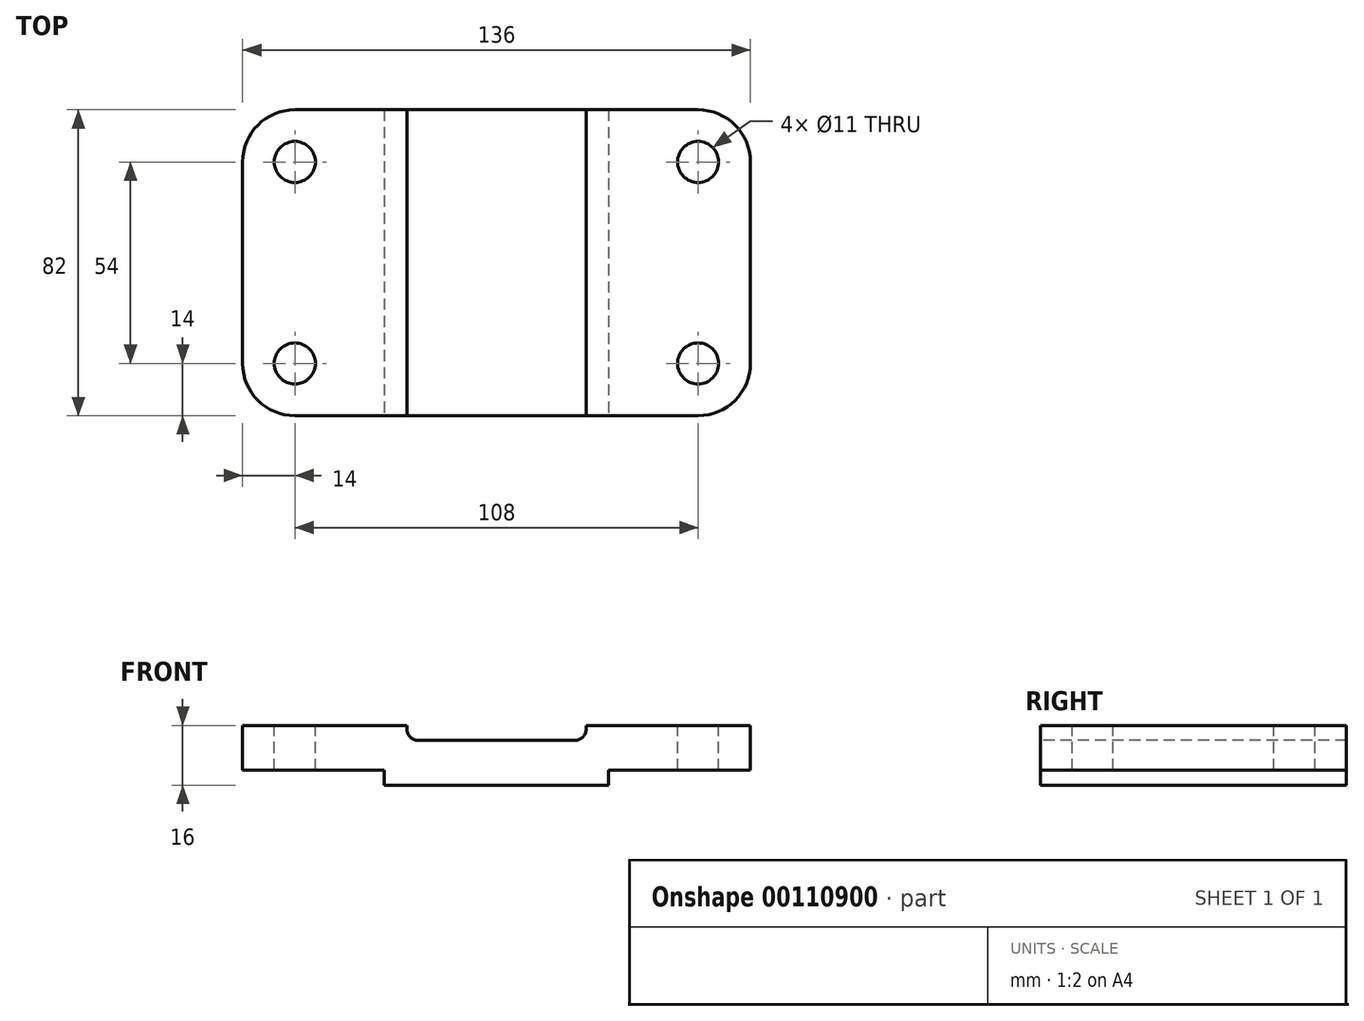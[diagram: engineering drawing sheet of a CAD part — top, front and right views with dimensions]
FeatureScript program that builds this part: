
annotation { "Feature Type Name" : "Feature", "Feature Type Description" : "" }
export const myFeature = defineFeature(function(context is Context, id is Id, definition is map)
    precondition{}
    {
        {
            var Q0;
            Q0=qCreatedBy(makeId("Top.planeOp"),FACE);
            var sketch = newSketch(context, id + "F0", { "sketchPlane" : qUnion([Q0])});
            skLineSegment(sketch, "E0.bottom", {"start": v(-14, 0) * mm, "end": v(-122, 0) * mm});
            skLineSegment(sketch, "E0.top", {"start": v(-14, 82) * mm, "end": v(-122, 82) * mm});
            skLineSegment(sketch, "E0.left", {"start": v(0, 14) * mm, "end": v(0, 68) * mm});
            skLineSegment(sketch, "E0.right", {"start": v(-136, 14) * mm, "end": v(-136, 68) * mm});
            skPoint(sketch, "E1.visualSharp", {"position": v(-136, 82) * mm});
            skArc(sketch, "E1.filletArc", {"start": v(-122, 82) * mm, "mid": v(-131.9, 77.9) * mm, "end": v(-136, 68) * mm});
            skPoint(sketch, "E2.visualSharp", {"position": v(0, 82) * mm});
            skArc(sketch, "E2.filletArc", {"start": v(0, 68) * mm, "mid": v(-4.1, 77.9) * mm, "end": v(-14, 82) * mm});
            skPoint(sketch, "E3.visualSharp", {"position": v(0, 0) * mm});
            skArc(sketch, "E3.filletArc", {"start": v(-14, 0) * mm, "mid": v(-4.1, 4.1) * mm, "end": v(0, 14) * mm});
            skPoint(sketch, "E4.visualSharp", {"position": v(-136, 0) * mm});
            skArc(sketch, "E4.filletArc", {"start": v(-136, 14) * mm, "mid": v(-131.9, 4.1) * mm, "end": v(-122, 0) * mm});
            skCircle(sketch, "E5", {"center": v(-122, 68) * mm, "radius": 5.5 * mm});
            skCircle(sketch, "E6.0.1.0", {"center": v(-122, 14) * mm, "radius": 5.5 * mm});
            skCircle(sketch, "E6.1.0.0", {"center": v(-14, 68) * mm, "radius": 5.5 * mm});
            skCircle(sketch, "E6.1.1.0", {"center": v(-14, 14) * mm, "radius": 5.5 * mm});
            skLineSegment(sketch, "E6.direction1", {"start": v(-122, 68) * mm, "end": v(-14, 68) * mm, "construction": true});
            skLineSegment(sketch, "E6.direction2", {"start": v(-122, 68) * mm, "end": v(-122, 14) * mm, "construction": true});
            skSolve(sketch);
        }
        {
            var Q0;
            Q0=makeQuery(id+"F0.imprint","IMPRINT",FACE,{"disambiguationData":[TD([[makeQuery(id+"F0.imprint","IMPRINT",EDGE,{"derivedFrom":sQuery(id+"F0.wireOp",EDGE,"E0.bottom")}),-1.0]])]});
            extrude(context, id + "F1", {"entities" : qUnion([Q0]), "oppositeDirection" : true, "depth" : 16 * mm});
        }
        {
            var Q0;
            Q0=makeQuery(id+"F1.opExtrude","SWEPT_FACE",FACE,{"disambiguationData":[OSD([sQuery(id+"F0.wireOp",EDGE,"E0.bottom")])]});
            var sketch = newSketch(context, id + "F2", { "sketchPlane" : qUnion([Q0])});
            skLineSegment(sketch, "E7", {"start": v(0, 0) * mm, "end": v(-44, 0) * mm});
            skLineSegment(sketch, "E8", {"start": v(-44, 0) * mm, "end": v(-44, -1) * mm});
            skLineSegment(sketch, "E9", {"start": v(-47, -4) * mm, "end": v(-89, -4) * mm});
            skLineSegment(sketch, "E10", {"start": v(-92, -1) * mm, "end": v(-92, 0) * mm});
            skLineSegment(sketch, "E11", {"start": v(-92, 0) * mm, "end": v(-136, 0) * mm});
            skPoint(sketch, "E12.visualSharp", {"position": v(-92, -4) * mm});
            skArc(sketch, "E12.filletArc", {"start": v(-92, -1) * mm, "mid": v(-91.12, -3.12) * mm, "end": v(-89, -4) * mm});
            skPoint(sketch, "E13.visualSharp", {"position": v(-44, -4) * mm});
            skArc(sketch, "E13.filletArc", {"start": v(-47, -4) * mm, "mid": v(-44.88, -3.12) * mm, "end": v(-44, -1) * mm});
            skLineSegment(sketch, "E14", {"start": v(-136, -12) * mm, "end": v(-98, -12) * mm});
            skLineSegment(sketch, "E15", {"start": v(-98, -12) * mm, "end": v(-98, -16) * mm});
            skLineSegment(sketch, "E16", {"start": v(-98, -16) * mm, "end": v(-38, -16) * mm});
            skLineSegment(sketch, "E17", {"start": v(-38, -16) * mm, "end": v(-38, -12) * mm});
            skLineSegment(sketch, "E18", {"start": v(-38, -12) * mm, "end": v(0, -12) * mm});
            skLineSegment(sketch, "E19", {"start": v(-136, 0) * mm, "end": v(-136, -12) * mm});
            skLineSegment(sketch, "E20", {"start": v(0, 0) * mm, "end": v(0, -12) * mm});
            skLineSegment(sketch, "E21", {"start": v(-136, -12) * mm, "end": v(-136, -16) * mm});
            skLineSegment(sketch, "E22", {"start": v(-136, -16) * mm, "end": v(-98, -16) * mm});
            skLineSegment(sketch, "E23", {"start": v(0, -12) * mm, "end": v(0, -16) * mm});
            skLineSegment(sketch, "E24", {"start": v(0, -16) * mm, "end": v(-38, -16) * mm});
            skLineSegment(sketch, "E25", {"start": v(-92, 0) * mm, "end": v(-44, 0) * mm});
            skSolve(sketch);
        }
        {
            var Q0;
            {var subQ0=sQuery(id+"F2.wireOp",EDGE,"E15");Q0=makeQuery(id+"F2.imprint","IMPRINT",FACE,{"disambiguationData":[TD([[makeQuery(id+"F2.imprint","IMPRINT",EDGE,{"derivedFrom":subQ0}),-1.0]])]});}
            var Q1;
            {var subQ0=sQuery(id+"F2.wireOp",EDGE,"E21");Q1=makeQuery(id+"F2.imprint","IMPRINT",FACE,{"disambiguationData":[TD([[makeQuery(id+"F2.imprint","IMPRINT",EDGE,{"derivedFrom":subQ0}),1.0]])]});}
            var Q2;
            {var subQ0=sQuery(id+"F2.wireOp",EDGE,"E17");Q2=makeQuery(id+"F2.imprint","IMPRINT",FACE,{"disambiguationData":[TD([[makeQuery(id+"F2.imprint","IMPRINT",EDGE,{"derivedFrom":subQ0}),-1.0]])]});}
            var Q3;
            {var subQ0=sQuery(id+"F2.wireOp",EDGE,"E23");Q3=makeQuery(id+"F2.imprint","IMPRINT",FACE,{"disambiguationData":[TD([[makeQuery(id+"F2.imprint","IMPRINT",EDGE,{"derivedFrom":subQ0}),-1.0]])]});}
            var Q4;
            Q4=makeQuery(id+"F2.imprint","IMPRINT",FACE,{"disambiguationData":[TD([[makeQuery(id+"F2.imprint","IMPRINT",EDGE,{"derivedFrom":sQuery(id+"F2.wireOp",EDGE,"E8")}),-1.0]])]});
            extrude(context, id + "F3", {"entities" : qUnion([Q0, Q1, Q2, Q3, Q4]), "operationType" : NewBodyOperationType.REMOVE, "endBound" : BoundingType.THROUGH_ALL, "oppositeDirection" : true, "depth" : 25 * mm});
        }
    });
